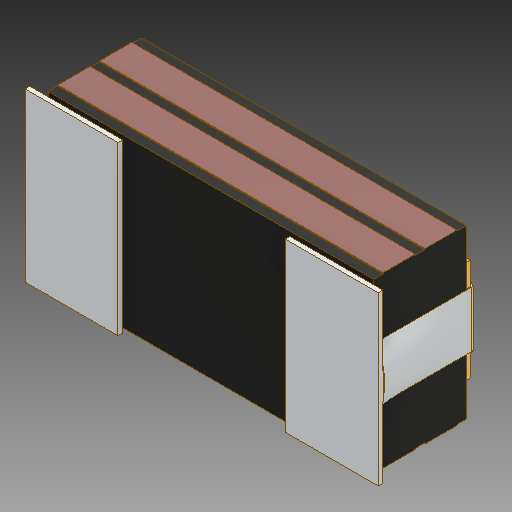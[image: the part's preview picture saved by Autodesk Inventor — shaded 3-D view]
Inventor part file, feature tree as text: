
AUTODESK INVENTOR PART (.ipt)
format: ipt  version: 2018 (Build 220112000, 112)  size: 258,048 bytes
history: native  units: mm
features: fillet x1
ambient origin geometry x8: Origin, YZ Plane, XZ Plane, XY Plane, X Axis, Y Axis, Z Axis, Center Point
bodies: Volumenkörper1 (feature_tree)
feature tree (1):
  fillet  "Fillet5"  [1 undecoded]
note: 1 required parameter value undecoded (feature->parameter linkage not recoverable at this tier; creation-order binding heuristic only, values carry confidence <= 0.55)
